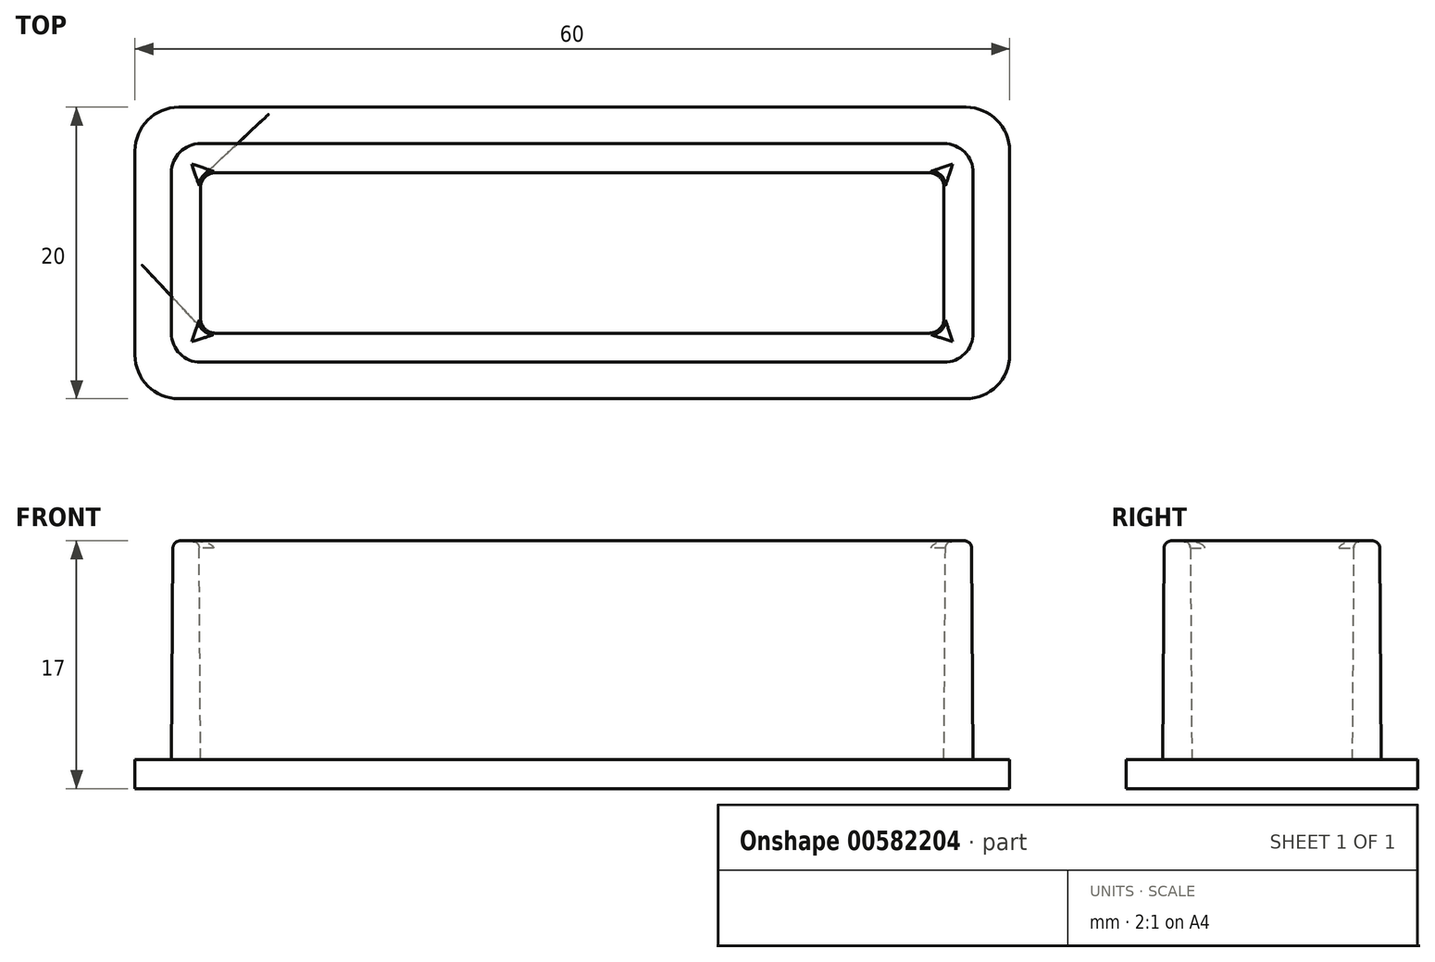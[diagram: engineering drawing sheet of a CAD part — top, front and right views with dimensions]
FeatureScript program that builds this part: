
annotation { "Feature Type Name" : "Feature", "Feature Type Description" : "" }
export const myFeature = defineFeature(function(context is Context, id is Id, definition is map)
    precondition{}
    {
        {
            var Q0;
            Q0=qCreatedBy(makeId("Top.planeOp"),FACE);
            var sketch = newSketch(context, id + "F0", { "sketchPlane" : qUnion([Q0])});
            skLineSegment(sketch, "E0.bottom", {"start": v(27, 10) * mm, "end": v(-27, 10) * mm});
            skLineSegment(sketch, "E0.top", {"start": v(27, -10) * mm, "end": v(-27, -10) * mm});
            skLineSegment(sketch, "E0.left", {"start": v(30, 7) * mm, "end": v(30, -7) * mm});
            skLineSegment(sketch, "E0.right", {"start": v(-30, 7) * mm, "end": v(-30, -7) * mm});
            skPoint(sketch, "E0.middle", {"position": v(0, 0) * mm});
            skPoint(sketch, "E1.visualSharp", {"position": v(-30, 10) * mm});
            skArc(sketch, "E1.filletArc", {"start": v(-27, 10) * mm, "mid": v(-29.12, 9.12) * mm, "end": v(-30, 7) * mm});
            skPoint(sketch, "E2.visualSharp", {"position": v(-30, -10) * mm});
            skArc(sketch, "E2.filletArc", {"start": v(-30, -7) * mm, "mid": v(-29.12, -9.12) * mm, "end": v(-27, -10) * mm});
            skPoint(sketch, "E3.visualSharp", {"position": v(30, -10) * mm});
            skArc(sketch, "E3.filletArc", {"start": v(27, -10) * mm, "mid": v(29.12, -9.12) * mm, "end": v(30, -7) * mm});
            skPoint(sketch, "E4.visualSharp", {"position": v(30, 10) * mm});
            skArc(sketch, "E4.filletArc", {"start": v(30, 7) * mm, "mid": v(29.12, 9.12) * mm, "end": v(27, 10) * mm});
            skLineSegment(sketch, "E5.0", {"start": v(25.5, 7.5) * mm, "end": v(-25.5, 7.5) * mm});
            skLineSegment(sketch, "E5.1", {"start": v(27.5, 5.5) * mm, "end": v(27.5, -5.5) * mm});
            skLineSegment(sketch, "E5.2", {"start": v(25.5, -7.5) * mm, "end": v(-25.5, -7.5) * mm});
            skLineSegment(sketch, "E5.3", {"start": v(-27.5, 5.5) * mm, "end": v(-27.5, -5.5) * mm});
            skPoint(sketch, "E6.visualSharp", {"position": v(27.5, 7.5) * mm});
            skArc(sketch, "E6.filletArc", {"start": v(27.5, 5.5) * mm, "mid": v(26.91, 6.91) * mm, "end": v(25.5, 7.5) * mm});
            skPoint(sketch, "E7.visualSharp", {"position": v(27.5, -7.5) * mm});
            skArc(sketch, "E7.filletArc", {"start": v(25.5, -7.5) * mm, "mid": v(26.91, -6.91) * mm, "end": v(27.5, -5.5) * mm});
            skPoint(sketch, "E8.visualSharp", {"position": v(-27.5, -7.5) * mm});
            skArc(sketch, "E8.filletArc", {"start": v(-27.5, -5.5) * mm, "mid": v(-26.91, -6.91) * mm, "end": v(-25.5, -7.5) * mm});
            skPoint(sketch, "E9.visualSharp", {"position": v(-27.5, 7.5) * mm});
            skArc(sketch, "E9.filletArc", {"start": v(-25.5, 7.5) * mm, "mid": v(-26.91, 6.91) * mm, "end": v(-27.5, 5.5) * mm});
            skLineSegment(sketch, "E10.0", {"start": v(25.5, 5.5) * mm, "end": v(-25.5, 5.5) * mm});
            skLineSegment(sketch, "E10.1", {"start": v(25.5, 5.5) * mm, "end": v(25.5, -5.5) * mm});
            skLineSegment(sketch, "E10.2", {"start": v(25.5, -5.5) * mm, "end": v(-25.5, -5.5) * mm});
            skLineSegment(sketch, "E10.3", {"start": v(-25.5, 5.5) * mm, "end": v(-25.5, -5.5) * mm});
            skSolve(sketch);
        }
        {
            var Q0;
            Q0=makeQuery(id+"F0.imprint","IMPRINT",FACE,{"disambiguationData":[TD([[makeQuery(id+"F0.imprint","IMPRINT",EDGE,{"derivedFrom":sQuery(id+"F0.wireOp",EDGE,"E5.0")}),1.0]])]});
            extrude(context, id + "F1", {"entities" : qUnion([Q0]), "depth" : 15 * mm, "offsetDistance" : 25 * mm, "hasDraft" : true, "draftAngle" : 0.4 * degree, "draftPullDirection" : true});
        }
        {
            var Q0;
            Q0 = qSketchRegion(id + "F0", true);
            var Q1;
            Q1=makeQuery(id+"F0.imprint","IMPRINT",FACE,{"disambiguationData":[TD([[makeQuery(id+"F0.imprint","IMPRINT",EDGE,{"derivedFrom":sQuery(id+"F0.wireOp",EDGE,"E5.0")}),1.0]])]});
            var Q2;
            Q2=makeQuery(id+"F0.imprint","IMPRINT",FACE,{"disambiguationData":[TD([[makeQuery(id+"F0.imprint","IMPRINT",EDGE,{"derivedFrom":sQuery(id+"F0.wireOp",EDGE,"E10.0")}),1.0]])]});
            extrude(context, id + "F2", {"entities" : qUnion([Q0, Q1, Q2]), "operationType" : NewBodyOperationType.ADD, "oppositeDirection" : true, "depth" : 2 * mm, "offsetDistance" : 25 * mm});
        }
        {
            var Q0;
            Q0=makeQuery(id+"F1.opExtrude","CAP_FACE",FACE,{"disambiguationData":[OSD([sQuery(id+"F0.wireOp",EDGE,"E5.0"),sQuery(id+"F0.wireOp",EDGE,"E5.1"),sQuery(id+"F0.wireOp",EDGE,"E5.2"),sQuery(id+"F0.wireOp",EDGE,"E5.3"),sQuery(id+"F0.wireOp",EDGE,"E6.filletArc"),sQuery(id+"F0.wireOp",EDGE,"E7.filletArc"),sQuery(id+"F0.wireOp",EDGE,"E8.filletArc"),sQuery(id+"F0.wireOp",EDGE,"E9.filletArc"),sQuery(id+"F0.wireOp",EDGE,"E10.0"),sQuery(id+"F0.wireOp",EDGE,"E10.1"),sQuery(id+"F0.wireOp",EDGE,"E10.2"),sQuery(id+"F0.wireOp",EDGE,"E10.3")])],"isStart":false});
            fillet(context, id + "F3", {"entities" : qUnion([Q0]), "radius" : 0.5 * mm, "tangentPropagation" : true, "allowEdgeOverflow" : false});
        }
        {
            var Q0;
            Q0=makeQuery(id+"F1.opExtrude","SWEPT_EDGE",EDGE,{"disambiguationData":[OSD([sQuery(id+"F0.wireOp",EDGE,"E10.0"),sQuery(id+"F0.wireOp",EDGE,"E10.1")])]});
            var Q1;
            Q1=makeQuery(id+"F1.opExtrude","SWEPT_EDGE",EDGE,{"disambiguationData":[OSD([sQuery(id+"F0.wireOp",EDGE,"E10.1"),sQuery(id+"F0.wireOp",EDGE,"E10.2")])]});
            var Q2;
            Q2=makeQuery(id+"F1.opExtrude","SWEPT_EDGE",EDGE,{"disambiguationData":[OSD([sQuery(id+"F0.wireOp",EDGE,"E10.0"),sQuery(id+"F0.wireOp",EDGE,"E10.3")])]});
            var Q3;
            Q3=makeQuery(id+"F1.opExtrude","SWEPT_EDGE",EDGE,{"disambiguationData":[OSD([sQuery(id+"F0.wireOp",EDGE,"E10.2"),sQuery(id+"F0.wireOp",EDGE,"E10.3")])]});
            fillet(context, id + "F4", {"entities" : qUnion([Q0, Q1, Q2, Q3]), "radius" : 1 * mm, "tangentPropagation" : true, "defaultsChanged" : false, "allowEdgeOverflow" : false, "vertexSettings" : [], "filletType" : FilletType.EDGE});
        }
    });
